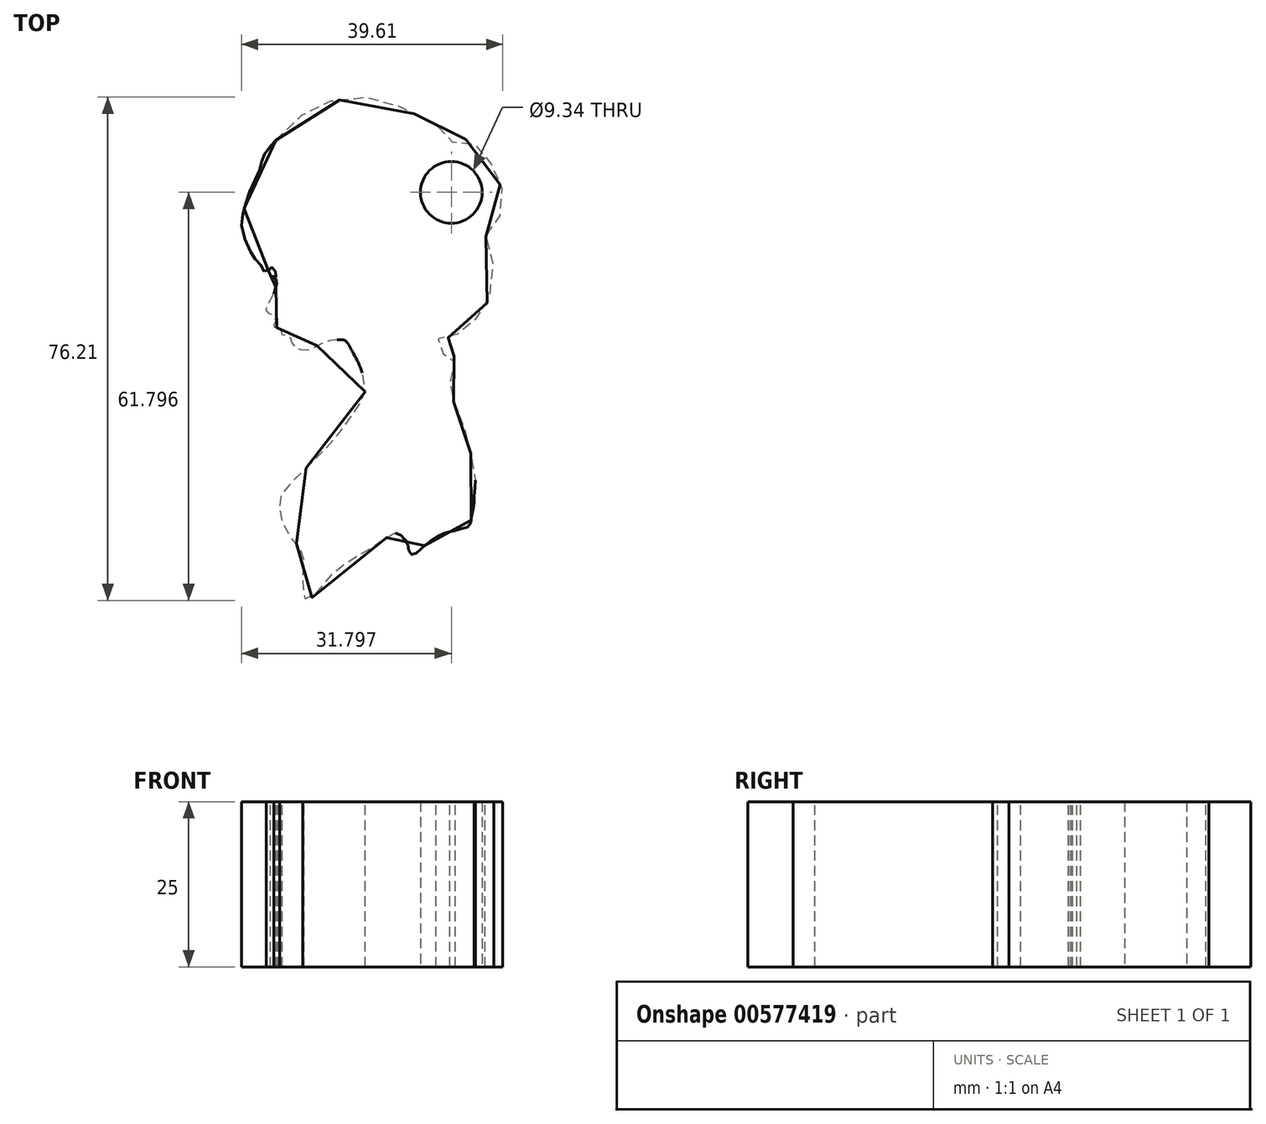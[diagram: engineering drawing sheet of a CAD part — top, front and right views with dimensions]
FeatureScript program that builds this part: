
annotation { "Feature Type Name" : "Feature", "Feature Type Description" : "" }
export const myFeature = defineFeature(function(context is Context, id is Id, definition is map)
    precondition{}
    {
        {
            var Q0;
            Q0=qCreatedBy(makeId("Top.planeOp"),FACE);
            var sketch = newSketch(context, id + "F0", { "sketchPlane" : qUnion([Q0])});
            skFitSpline(sketch, "E0", {"points": [v(-53.02, 80.1) * mm, v(-51.18, 82.03) * mm, v(-49.87, 83.13) * mm, v(-48.17, 84.63) * mm, v(-46.65, 85.3) * mm, v(-45.2, 85.91) * mm, v(-42.5, 86.31) * mm, v(-41, 86.54) * mm, v(-38.79, 86.58) * mm, v(-37.23, 86.33) * mm, v(-34.9, 85.48) * mm, v(-32.63, 84.4) * mm, v(-30.07, 83.03) * mm, v(-27.92, 82.03) * mm, v(-27.15, 81.08) * mm, v(-26.9, 80.33) * mm, v(-26.39, 79.84) * mm, v(-25.8, 79.94) * mm, v(-25.02, 80.24) * mm, v(-23.86, 80.1) * mm, v(-22.87, 79.46) * mm, v(-22, 78.6) * mm, v(-21.21, 77.64) * mm, v(-20.59, 76.88) * mm, v(-20.1, 75.8) * mm, v(-19.39, 74.56) * mm, v(-19.11, 73.5) * mm, v(-18.65, 72.42) * mm, v(-18.74, 71.1) * mm, v(-18.82, 69.98) * mm, v(-19.15, 68.57) * mm, v(-19.9, 67.38) * mm, v(-20.63, 66.38) * mm, v(-21.28, 65.88) * mm, v(-20.95, 65.03) * mm, v(-20.6, 63.49) * mm, v(-20.42, 62.02) * mm, v(-20.01, 61.04) * mm, v(-20.45, 57.81) * mm, v(-20.56, 56.87) * mm, v(-20.86, 55.77) * mm, v(-21.55, 54.73) * mm, v(-22.3, 53.69) * mm, v(-23, 52.69) * mm, v(-23.83, 51.86) * mm, v(-24.77, 51.08) * mm, v(-25.12, 50.79) * mm, v(-25.68, 50.69) * mm, v(-26.57, 50.33) * mm, v(-27.17, 50.04) * mm, v(-27.58, 49.97) * mm, v(-28.3, 50) * mm, v(-28.63, 50.01) * mm, v(-28.72, 49.47) * mm, v(-28.4, 49) * mm, v(-28.05, 48.32) * mm, v(-27.66, 47.78) * mm, v(-27.4, 47.46) * mm, v(-26.88, 47.52) * mm, v(-26.27, 47.4) * mm, v(-25.87, 47.3) * mm, v(-25.93, 46.83) * mm, v(-26.17, 46.02) * mm, v(-26.38, 45.2) * mm, v(-26.55, 44.4) * mm, v(-26.65, 43.34) * mm, v(-26.6, 42.66) * mm, v(-26.54, 41.95) * mm, v(-26.32, 41.12) * mm, v(-26, 40.25) * mm, v(-25.59, 39.5) * mm, v(-25.16, 38.48) * mm, v(-24.79, 37.61) * mm, v(-24.54, 36.7) * mm, v(-24.4, 36.08) * mm, v(-24.08, 35.12) * mm, v(-23.84, 34.04) * mm, v(-23.4, 32.33) * mm, v(-23.01, 30.94) * mm, v(-22.88, 29.5) * mm, v(-22.8, 27.84) * mm, v(-23.02, 25.84) * mm, v(-23, 24.67) * mm, v(-23.38, 22.95) * mm, v(-23.68, 21.7) * mm, v(-24.98, 21.22) * mm, v(-26.25, 20.85) * mm, v(-26.97, 20.72) * mm, v(-27.83, 20.42) * mm, v(-28.66, 19.96) * mm, v(-29.46, 19.42) * mm, v(-30.33, 18.78) * mm, v(-31.25, 17.96) * mm, v(-32.14, 17.3) * mm, v(-32.75, 17.6) * mm, v(-32.99, 18.68) * mm, v(-33.45, 19.6) * mm, v(-34.28, 20.4) * mm, v(-35.28, 20.55) * mm, v(-36.21, 19.94) * mm, v(-37.55, 18.92) * mm, v(-39.78, 17.63) * mm, v(-42.63, 15.83) * mm, v(-45.1, 13.76) * mm, v(-48.1, 10.41) * mm, v(-48.6, 10.68) * mm, v(-48.76, 11.78) * mm, v(-48.91, 13.13) * mm, v(-48.8, 15.17) * mm, v(-48.78, 16.99) * mm, v(-49.3, 18.2) * mm, v(-50.79, 20.04) * mm, v(-52.04, 22.26) * mm, v(-52.4, 24.37) * mm, v(-52.3, 26.06) * mm, v(-49.98, 28.93) * mm, v(-46.54, 32.3) * mm, v(-44.15, 34.85) * mm, v(-42.15, 37.46) * mm, v(-40.24, 40.26) * mm, v(-39.48, 42) * mm, v(-40.09, 45.36) * mm, v(-41.76, 48.71) * mm, v(-42.47, 49.71) * mm, v(-43.75, 49.87) * mm, v(-45.96, 49.36) * mm, v(-48.3, 48.26) * mm, v(-49.95, 48.69) * mm, v(-50.63, 49.57) * mm, v(-50.95, 50.3) * mm, v(-51.93, 50.57) * mm, v(-52.1, 50.65) * mm, v(-52.1, 51.02) * mm, v(-52.14, 51.34) * mm, v(-52.61, 51.63) * mm, v(-53.07, 51.73) * mm, v(-53.22, 51.74) * mm, v(-53.27, 52.18) * mm, v(-53.03, 52.72) * mm, v(-53.08, 53.02) * mm, v(-53.28, 53.46) * mm, v(-54, 53.82) * mm, v(-54.45, 54.3) * mm, v(-54.23, 55.22) * mm, v(-53.47, 56.55) * mm, v(-52.8, 58.66) * mm, v(-52.86, 59.06) * mm, v(-53.3, 59) * mm, v(-53.68, 59.34) * mm, v(-53.85, 59.63) * mm, v(-53.57, 59.46) * mm, v(-53.12, 59.4) * mm, v(-52.96, 59.49) * mm, v(-53.02, 60) * mm, v(-53.38, 60.75) * mm, v(-53.8, 60.78) * mm, v(-54, 60.47) * mm, v(-54.5, 60.25) * mm, v(-54.91, 60.31) * mm, v(-55.09, 60.86) * mm, v(-56.16, 62.08) * mm, v(-57, 63.5) * mm, v(-58.2, 67.04) * mm, v(-57.88, 69.44) * mm, v(-57.08, 72.1) * mm, v(-55.74, 74.95) * mm, v(-55.23, 76.5) * mm, v(-54.94, 77.65) * mm, v(-53.72, 79.28) * mm, v(-53.02, 80.1) * mm]});
            skCircle(sketch, "E1", {"center": v(-26.43, 72.19) * mm, "radius": 4.67 * mm});
            skSolve(sketch);
        }
        {
            var Q0;
            Q0 = qSketchRegion(id + "F0", true);
            extrude(context, id + "F1", {"entities" : qUnion([Q0]), "depth" : 5 * mm, "offsetDistance" : 25 * mm});
        }
        {
            var Q0;
            Q0 = qSketchRegion(id + "F0", true);
            extrude(context, id + "F2", {"entities" : qUnion([Q0]), "operationType" : NewBodyOperationType.ADD, "depth" : 25 * mm, "offsetDistance" : 25 * mm});
        }
    });
